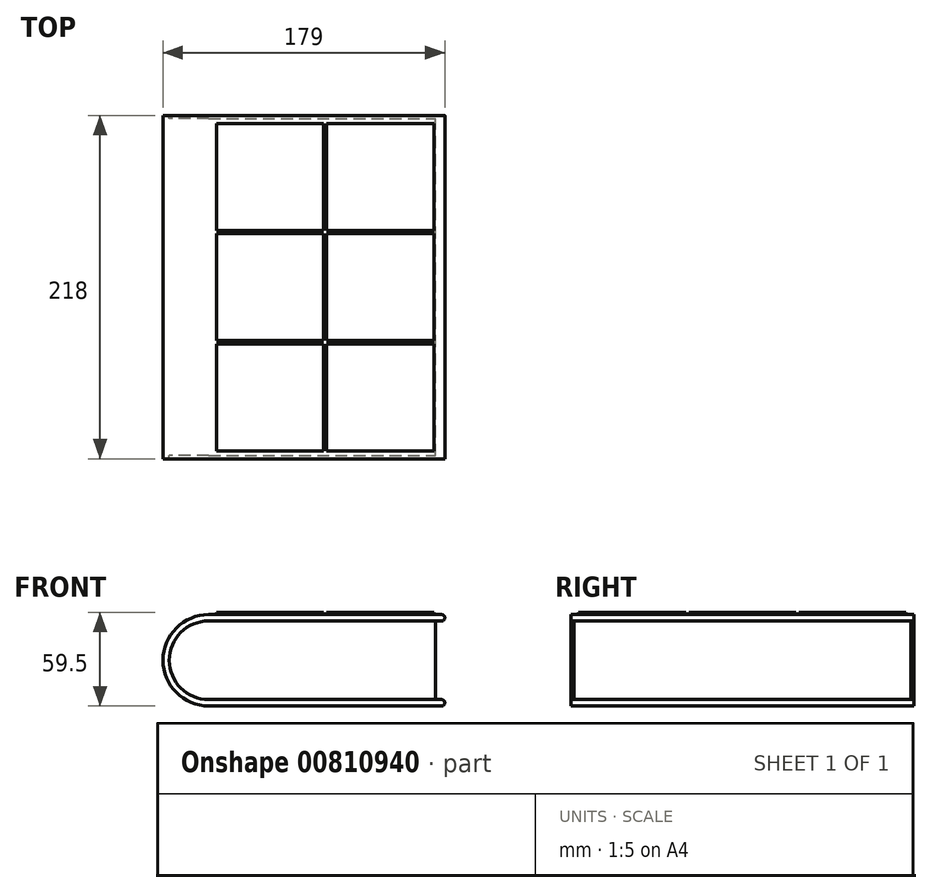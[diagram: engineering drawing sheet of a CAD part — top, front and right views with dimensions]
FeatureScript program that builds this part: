
annotation { "Feature Type Name" : "Feature", "Feature Type Description" : "" }
export const myFeature = defineFeature(function(context is Context, id is Id, definition is map)
    precondition{}
    {
        {
            var Q0;
            Q0=qCreatedBy(makeId("Front.planeOp"),FACE);
            var sketch = newSketch(context, id + "F0", { "sketchPlane" : qUnion([Q0])});
            skLineSegment(sketch, "E0", {"start": v(0, 25) * mm, "end": v(148, 25) * mm});
            skLineSegment(sketch, "E1", {"start": v(148, -25) * mm, "end": v(0, -25) * mm});
            skArc(sketch, "E2", {"start": v(0, 25) * mm, "mid": v(-25, 0) * mm, "end": v(0, -25) * mm});
            skLineSegment(sketch, "E3.0", {"start": v(0, 29) * mm, "end": v(148, 29) * mm});
            skArc(sketch, "E3.1", {"start": v(0, 29) * mm, "mid": v(-29, 0) * mm, "end": v(0, -29) * mm});
            skLineSegment(sketch, "E3.2", {"start": v(148, -29) * mm, "end": v(0, -29) * mm});
            skArc(sketch, "E4", {"start": v(148, 25) * mm, "mid": v(150, 27) * mm, "end": v(148, 29) * mm});
            skArc(sketch, "E5", {"start": v(148, -29) * mm, "mid": v(150, -27) * mm, "end": v(148, -25) * mm});
            skSolve(sketch);
        }
        {
            var Q0;
            Q0 = qSketchRegion(id + "F0", true);
            extrude(context, id + "F1", {"entities" : qUnion([Q0]), "endBound" : BoundingType.SYMMETRIC, "depth" : 218 * mm, "offsetDistance" : 25 * mm});
        }
        {
            var Q0;
            Q0=qCreatedBy(makeId("Front.planeOp"),FACE);
            var sketch = newSketch(context, id + "F2", { "sketchPlane" : qUnion([Q0])});
            skLineSegment(sketch, "E6", {"start": v(0, 0) * mm, "end": v(0, 25) * mm});
            skLineSegment(sketch, "E7", {"start": v(0, 25) * mm, "end": v(144, 25) * mm});
            skLineSegment(sketch, "E8", {"start": v(144, 25) * mm, "end": v(144, -25) * mm});
            skLineSegment(sketch, "E9", {"start": v(144, -25) * mm, "end": v(0, -25) * mm});
            skArc(sketch, "E10", {"start": v(0, 25) * mm, "mid": v(-25, 0) * mm, "end": v(0, -25) * mm});
            skSolve(sketch);
        }
        {
            var Q0;
            Q0 = qSketchRegion(id + "F2", true);
            extrude(context, id + "F3", {"entities" : qUnion([Q0]), "operationType" : NewBodyOperationType.ADD, "endBound" : BoundingType.SYMMETRIC, "depth" : 214 * mm, "offsetDistance" : 25 * mm});
        }
        {
            var Q0;
            Q0=makeQuery(id+"F1.opExtrude","SWEPT_FACE",FACE,{"disambiguationData":[OSD([sQuery(id+"F0.wireOp",EDGE,"E3.0")])]});
            var sketch = newSketch(context, id + "F4", { "sketchPlane" : qUnion([Q0])});
            skLineSegment(sketch, "E11.bottom", {"start": v(5, 104) * mm, "end": v(73, 104) * mm});
            skLineSegment(sketch, "E11.top", {"start": v(5, 36) * mm, "end": v(73, 36) * mm});
            skLineSegment(sketch, "E11.left", {"start": v(5, 104) * mm, "end": v(5, 36) * mm});
            skLineSegment(sketch, "E11.right", {"start": v(73, 104) * mm, "end": v(73, 36) * mm});
            skLineSegment(sketch, "E12.0.1.0", {"start": v(5, 34) * mm, "end": v(73, 34) * mm});
            skLineSegment(sketch, "E12.0.1.1", {"start": v(5, -34) * mm, "end": v(73, -34) * mm});
            skLineSegment(sketch, "E12.0.1.2", {"start": v(73, 34) * mm, "end": v(73, -34) * mm});
            skLineSegment(sketch, "E12.0.1.3", {"start": v(5, 34) * mm, "end": v(5, -34) * mm});
            skLineSegment(sketch, "E12.0.2.0", {"start": v(5, -36) * mm, "end": v(73, -36) * mm});
            skLineSegment(sketch, "E12.0.2.1", {"start": v(5, -104) * mm, "end": v(73, -104) * mm});
            skLineSegment(sketch, "E12.0.2.2", {"start": v(73, -36) * mm, "end": v(73, -104) * mm});
            skLineSegment(sketch, "E12.0.2.3", {"start": v(5, -36) * mm, "end": v(5, -104) * mm});
            skLineSegment(sketch, "E12.1.0.0", {"start": v(75, 104) * mm, "end": v(143, 104) * mm});
            skLineSegment(sketch, "E12.1.0.1", {"start": v(75, 36) * mm, "end": v(143, 36) * mm});
            skLineSegment(sketch, "E12.1.0.2", {"start": v(143, 104) * mm, "end": v(143, 36) * mm});
            skLineSegment(sketch, "E12.1.0.3", {"start": v(75, 104) * mm, "end": v(75, 36) * mm});
            skLineSegment(sketch, "E12.1.1.0", {"start": v(75, 34) * mm, "end": v(143, 34) * mm});
            skLineSegment(sketch, "E12.1.1.1", {"start": v(75, -34) * mm, "end": v(143, -34) * mm});
            skLineSegment(sketch, "E12.1.1.2", {"start": v(143, 34) * mm, "end": v(143, -34) * mm});
            skLineSegment(sketch, "E12.1.1.3", {"start": v(75, 34) * mm, "end": v(75, -34) * mm});
            skLineSegment(sketch, "E12.1.2.0", {"start": v(75, -36) * mm, "end": v(143, -36) * mm});
            skLineSegment(sketch, "E12.1.2.1", {"start": v(75, -104) * mm, "end": v(143, -104) * mm});
            skLineSegment(sketch, "E12.1.2.2", {"start": v(143, -36) * mm, "end": v(143, -104) * mm});
            skLineSegment(sketch, "E12.1.2.3", {"start": v(75, -36) * mm, "end": v(75, -104) * mm});
            skLineSegment(sketch, "E12.direction1", {"start": v(5, 36) * mm, "end": v(75, 36) * mm, "construction": true});
            skSolve(sketch);
        }
        {
            var Q0;
            Q0 = qSketchRegion(id + "F4", true);
            extrude(context, id + "F5", {"entities" : qUnion([Q0]), "operationType" : NewBodyOperationType.ADD, "depth" : 1.5 * mm, "offsetDistance" : 25 * mm});
        }
    });
